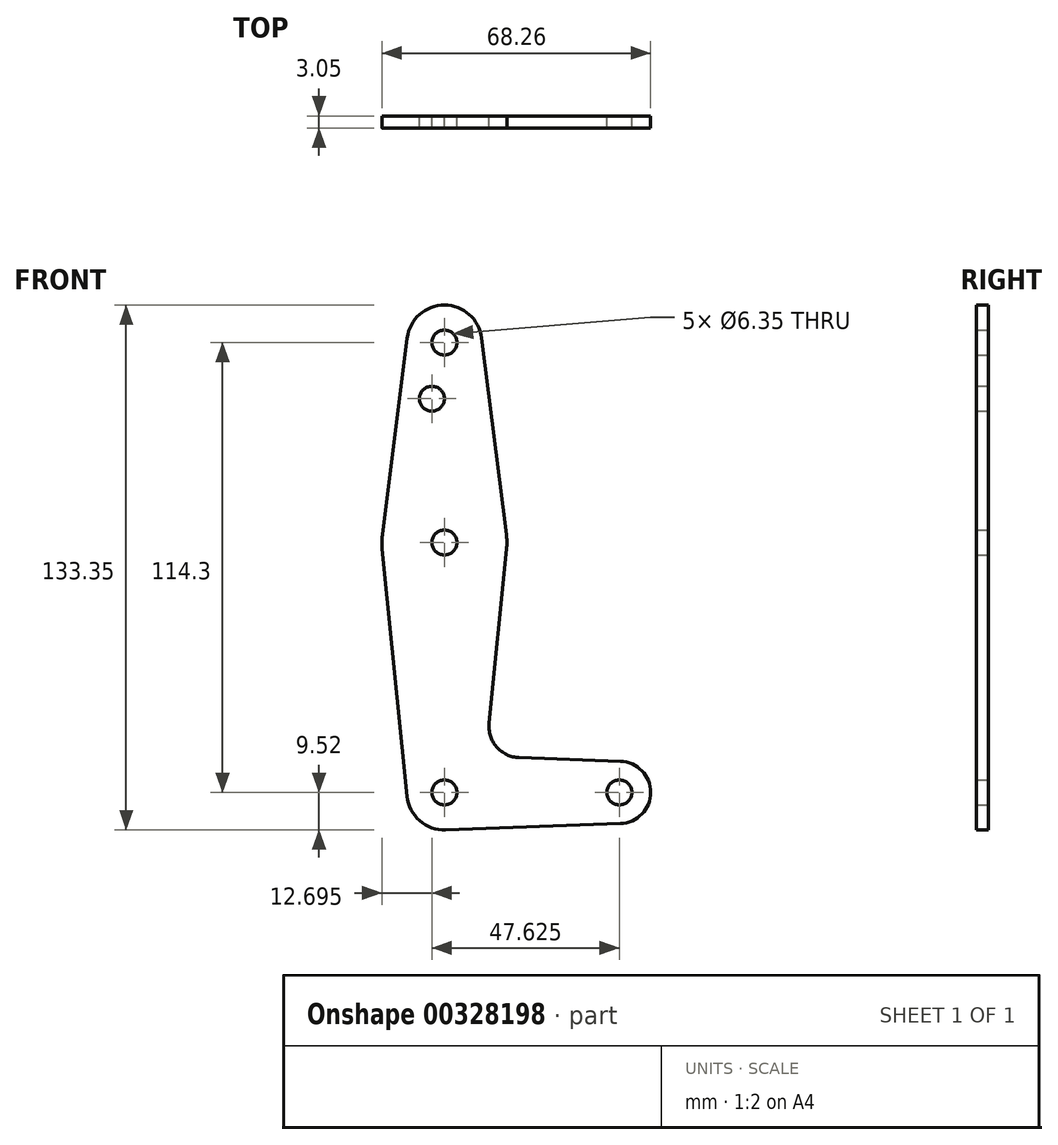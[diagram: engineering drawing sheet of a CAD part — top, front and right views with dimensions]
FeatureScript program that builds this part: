
annotation { "Feature Type Name" : "Feature", "Feature Type Description" : "" }
export const myFeature = defineFeature(function(context is Context, id is Id, definition is map)
    precondition{}
    {
        {
            var Q0;
            Q0=qCreatedBy(makeId("Front.planeOp"),FACE);
            var sketch = newSketch(context, id + "F0", { "sketchPlane" : qUnion([Q0])});
            skLineSegment(sketch, "E0", {"start": v(0, 0) * mm, "end": v(0, 114.3) * mm, "construction": true});
            skLineSegment(sketch, "E1", {"start": v(0, 0) * mm, "end": v(44.45, 0) * mm, "construction": true});
            skCircle(sketch, "E2", {"center": v(0, 114.3) * mm, "radius": 9.53 * mm});
            skCircle(sketch, "E3", {"center": v(0, 63.5) * mm, "radius": 15.88 * mm});
            skCircle(sketch, "E4", {"center": v(0, 0) * mm, "radius": 9.53 * mm});
            skCircle(sketch, "E5", {"center": v(44.45, 0) * mm, "radius": 7.94 * mm});
            skCircle(sketch, "E6", {"center": v(0, 0) * mm, "radius": 3.18 * mm});
            skLineSegment(sketch, "E7", {"start": v(-9.45, 115.5) * mm, "end": v(-15.75, 65.48) * mm});
            skLineSegment(sketch, "E8", {"start": v(44.73, -7.93) * mm, "end": v(0.34, -9.52) * mm});
            skLineSegment(sketch, "E9.MirrorCS", {"start": v(9.45, 115.5) * mm, "end": v(15.75, 65.48) * mm});
            skCircle(sketch, "E10", {"center": v(0, 63.5) * mm, "radius": 3.18 * mm});
            skCircle(sketch, "E11", {"center": v(-3.18, 100.03) * mm, "radius": 3.18 * mm});
            skCircle(sketch, "E12", {"center": v(44.45, 0) * mm, "radius": 3.18 * mm});
            skCircle(sketch, "E13", {"center": v(0, 114.3) * mm, "radius": 3.18 * mm});
            skLineSegment(sketch, "E14", {"start": v(-9.48, -0.95) * mm, "end": v(-15.8, 61.91) * mm});
            skLineSegment(sketch, "E15.MirrorCS", {"start": v(11.34, 17.6) * mm, "end": v(15.8, 61.91) * mm});
            skLineSegment(sketch, "E16.MirrorCS", {"start": v(0, 0) * mm, "end": v(-44.45, 0) * mm});
            skLineSegment(sketch, "E17.MirrorCS", {"start": v(44.73, 7.93) * mm, "end": v(18.97, 8.85) * mm});
            skArc(sketch, "E18.filletArc", {"start": v(11.34, 17.6) * mm, "mid": v(13.26, 11.57) * mm, "end": v(18.97, 8.85) * mm});
            skSolve(sketch);
        }
        {
            var Q0;
            Q0 = qSketchRegion(id + "F0", true);
            extrude(context, id + "F1", {"entities" : qUnion([Q0]), "depth" : 3.05 * mm});
        }
    });
